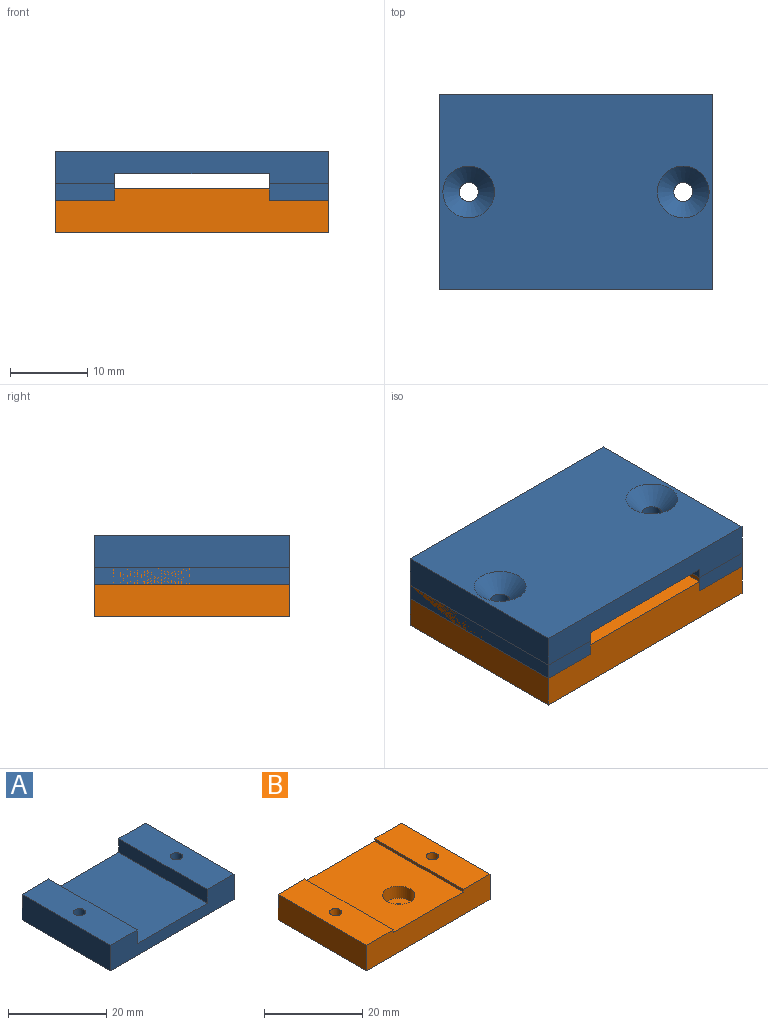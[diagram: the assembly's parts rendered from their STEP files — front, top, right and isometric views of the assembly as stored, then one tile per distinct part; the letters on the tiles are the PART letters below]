
ASSEMBLY  parts=2 mates=1
PART A: 14 faces, bbox 35.6x25.4x6.4 mm
  f0: plane 35.56x6.35mm, normal (0,1,0), area 156.8mm2, adj f1,f3,f4,f5,f6,f7,f8,f9
  f1: plane 25.4x6.35mm, normal (-1,0,0), area 161.3mm2, adj f0,f2,f4,f5
  f2: plane 35.56x6.35mm, normal (0,-1,0), area 156.8mm2, adj f1,f3,f4,f5,f6,f7,f8,f9
  f3: plane 25.4x3.43mm, normal (1,0,0), area 87.1mm2, adj f0,f2,f4,f9
  f4: plane 25.4x7.72mm, normal (0,0,1), area 191.2mm2, adj f0,f1,f2,f3,f12
  f5: plane 35.56x25.4mm, normal (0,0,-1), area 832.3mm2, adj f0,f1,f2,f7,f11,f13
  f6: plane 25.4x3.43mm, normal (-1,0,0), area 87.1mm2, adj f0,f2,f8,f9
  f7: plane 25.4x6.35mm, normal (1,0,0), area 161.3mm2, adj f0,f2,f5,f8
  f8: plane 25.4x7.72mm, normal (0,0,1), area 191.2mm2, adj f0,f2,f6,f7,f10
  f9: plane 25.4x20.12mm, normal (0,0,1), area 511mm2, adj f0,f2,f3,f6
  f10: cylinder r=1.25mm len=4.24mm, axis (0,0,-1), area 33.3mm2, adj f8,f11
  f11: cone r=1.25mm half-angle=45deg, axis (0,0,-1), area 43.2mm2, adj f5,f10
  f12: cylinder r=1.25mm len=4.24mm, axis (0,0,-1), area 33.3mm2, adj f4,f13
  f13: cone r=1.25mm half-angle=45deg, axis (0,0,-1), area 43.2mm2, adj f5,f12
PART B: 15 faces, bbox 35.6x25.4x6.4 mm
  f0: plane 35.56x6.35mm, normal (0,1,0), area 213mm2, adj f1,f3,f4,f5,f6,f7,f8,f9
  f1: plane 25.4x6.35mm, normal (-1,0,0), area 161.3mm2, adj f0,f2,f4,f5
  f2: plane 35.56x6.35mm, normal (0,-1,0), area 213mm2, adj f1,f3,f4,f5,f6,f7,f8,f9
  f3: plane 25.4x0.64mm, normal (1,0,0), area 16.1mm2, adj f0,f2,f4,f6
  f4: plane 25.4x7.72mm, normal (0,0,1), area 191.2mm2, adj f0,f1,f2,f3,f13
  f5: plane 35.56x25.4mm, normal (0,0,-1), area 888.5mm2, adj f0,f1,f2,f8,f10,f13,f14
  f6: plane 25.4x20.12mm, normal (0,0,1), area 477.8mm2, adj f0,f2,f3,f7,f12
  f7: plane 25.4x0.64mm, normal (-1,0,0), area 16.1mm2, adj f0,f2,f6,f9
  f8: plane 25.4x6.35mm, normal (1,0,0), area 161.3mm2, adj f0,f2,f5,f9
  f9: plane 25.4x7.72mm, normal (0,0,1), area 191.2mm2, adj f0,f2,f7,f8,f14
  f10: cylinder r=1.25mm len=2.72mm, axis (0,0,1), area 21.3mm2, adj f5,f11
  f11: plane 6.5x6.5mm, normal (0,0,1), area 28.3mm2, adj f10,f12
  f12: cylinder r=3.25mm len=6.5mm, axis (0,0,1), area 61.3mm2, adj f6,f11
  f13: cylinder r=1.25mm len=6.35mm, axis (0,0,1), area 49.9mm2, adj f4,f5
  f14: cylinder r=1.25mm len=6.35mm, axis (0,0,1), area 49.9mm2, adj f5,f9
PLACE A rot(axis=(1,0,0),180deg) t=(-0.46,-14.02,5.82)mm
PLACE B t=(-0.46,11.38,-4.76)mm
MATE fastened A.f10 <-> B.f14  axis (0,0,1) through (13.46,-1.32,1.59)mm
